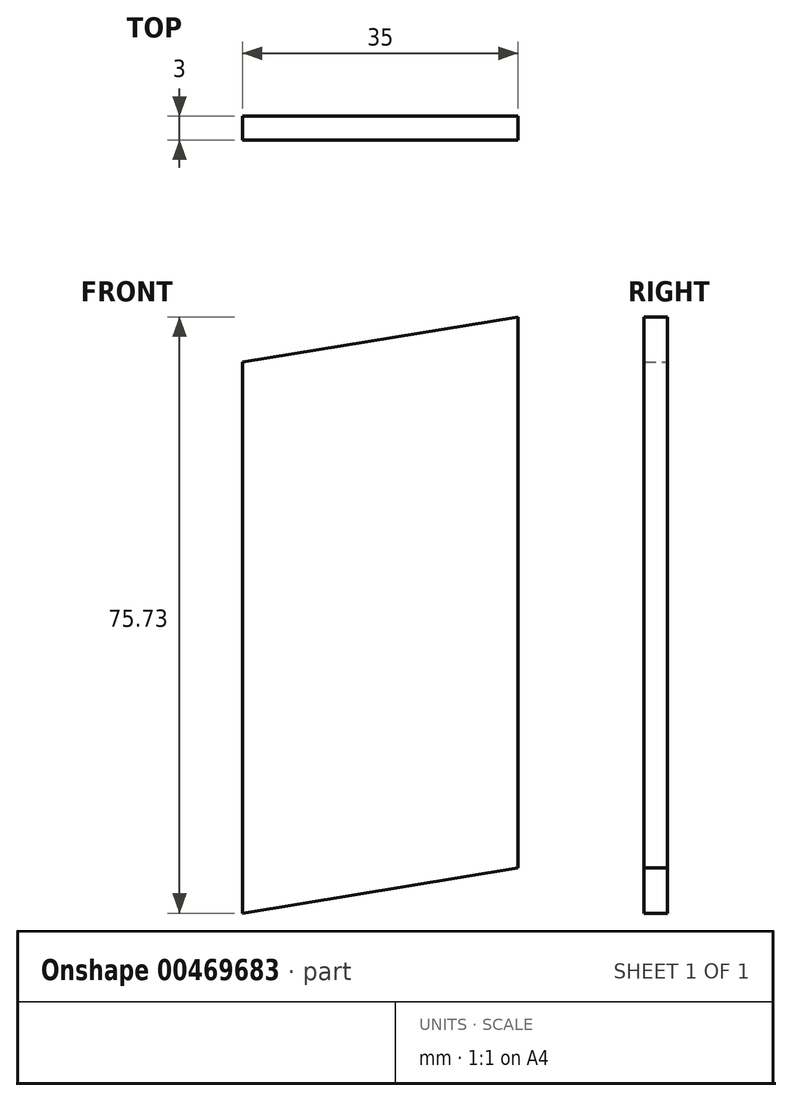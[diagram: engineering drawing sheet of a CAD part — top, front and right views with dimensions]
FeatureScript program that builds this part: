
annotation { "Feature Type Name" : "Feature", "Feature Type Description" : "" }
export const myFeature = defineFeature(function(context is Context, id is Id, definition is map)
    precondition{}
    {
        {
            var Q0;
            Q0=qCreatedBy(makeId("Front.planeOp"),FACE);
            var sketch = newSketch(context, id + "F0", { "sketchPlane" : qUnion([Q0])});
            skLineSegment(sketch, "E0", {"start": v(0, 0) * mm, "end": v(0, 35) * mm, "construction": true});
            skLineSegment(sketch, "E1", {"start": v(0, 0) * mm, "end": v(35, 0) * mm});
            skLineSegment(sketch, "E2.MirrorCS", {"start": v(0, 0) * mm, "end": v(-35, 0) * mm});
            skLineSegment(sketch, "E3", {"start": v(-35, 0) * mm, "end": v(-35, 35) * mm, "construction": true});
            skLineSegment(sketch, "E4", {"start": v(-35, 35) * mm, "end": v(-40.73, 35) * mm});
            skLineSegment(sketch, "E5", {"start": v(-40.73, 35) * mm, "end": v(-35, 0) * mm});
            skLineSegment(sketch, "E6", {"start": v(-40.73, 35) * mm, "end": v(29.27, 35) * mm});
            skPoint(sketch, "E6.endSnap0", {"position": v(-37.87, 35) * mm});
            skLineSegment(sketch, "E7", {"start": v(29.27, 35) * mm, "end": v(35, 0) * mm});
            skSolve(sketch);
        }
        {
            var Q0;
            Q0=makeQuery(id+"F0.imprint","IMPRINT",FACE,{"disambiguationData":[TD([[makeQuery(id+"F0.imprint","IMPRINT",EDGE,{"derivedFrom":sQuery(id+"F0.wireOp",EDGE,"E1")}),1.0]])]});
            extrude(context, id + "F1", {"entities" : qUnion([Q0]), "depth" : 3 * mm});
        }
        {
            var Q0;
            Q0=makeQuery(id+"F1.opExtrude","SWEPT_BODY",BODY,{"disambiguationData":[OSD([sQuery(id+"F0.wireOp",EDGE,"E1"),sQuery(id+"F0.wireOp",EDGE,"E2.MirrorCS"),sQuery(id+"F0.wireOp",EDGE,"E5"),sQuery(id+"F0.wireOp",EDGE,"E6"),sQuery(id+"F0.wireOp",EDGE,"E7")])]});
            var Q1;
            Q1=makeQuery(id+"F1.opExtrude","SWEPT_EDGE",EDGE,{"disambiguationData":[OSD([sQuery(id+"F0.wireOp",EDGE,"E2.MirrorCS"),sQuery(id+"F0.wireOp",EDGE,"E5")])]});
            transform(context, id + "F2", {"entities" : qUnion([Q0]), "transformType" : TransformType.ROTATION, "transformAxis" : qUnion([Q1]), "angle" : 90 * degree, "makeCopy" : false});
        }
    });
